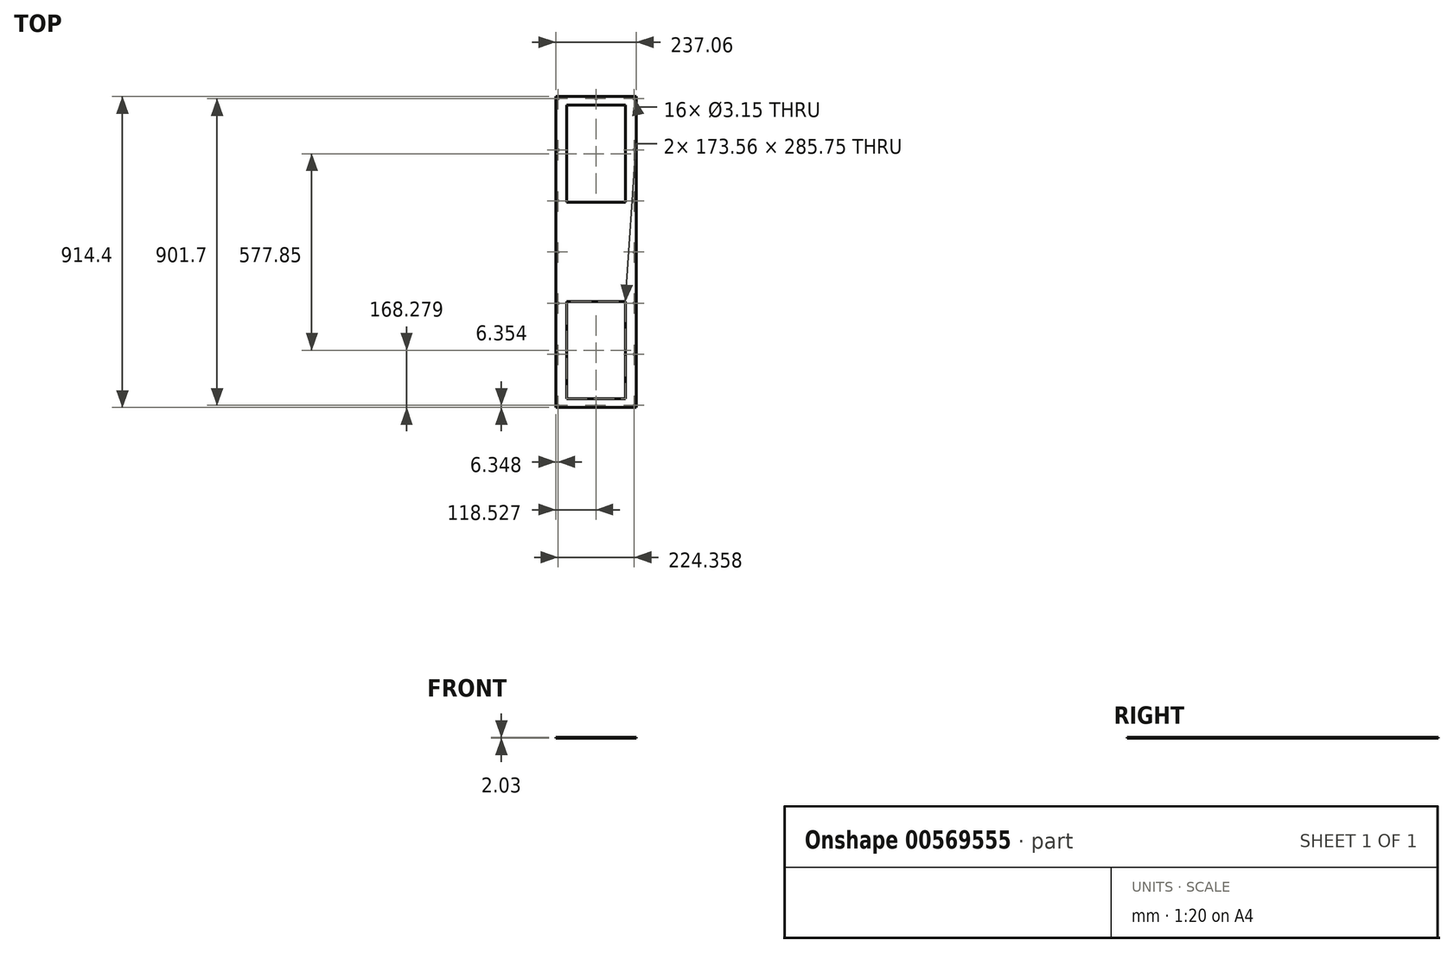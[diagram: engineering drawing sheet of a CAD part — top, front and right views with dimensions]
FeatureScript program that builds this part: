
annotation { "Feature Type Name" : "Feature", "Feature Type Description" : "" }
export const myFeature = defineFeature(function(context is Context, id is Id, definition is map)
    precondition{}
    {
        {
            var Q0;
            Q0=qCreatedBy(makeId("Top.planeOp"),FACE);
            var sketch = newSketch(context, id + "F0", { "sketchPlane" : qUnion([Q0])});
            skLineSegment(sketch, "E0.bottom", {"start": v(-468.83, 456.62) * mm, "end": v(-231.77, 456.62) * mm});
            skLineSegment(sketch, "E0.top", {"start": v(-468.83, -457.78) * mm, "end": v(-231.77, -457.78) * mm});
            skLineSegment(sketch, "E0.left", {"start": v(-468.83, 456.62) * mm, "end": v(-468.83, -457.78) * mm});
            skLineSegment(sketch, "E0.right", {"start": v(-231.77, 456.62) * mm, "end": v(-231.77, -457.78) * mm});
            skLineSegment(sketch, "E1.bottom", {"start": v(-437.08, 431.22) * mm, "end": v(-263.52, 431.22) * mm});
            skLineSegment(sketch, "E1.top", {"start": v(-437.08, 145.47) * mm, "end": v(-263.52, 145.47) * mm});
            skLineSegment(sketch, "E1.left", {"start": v(-437.08, 431.22) * mm, "end": v(-437.08, 145.47) * mm});
            skLineSegment(sketch, "E1.right", {"start": v(-263.52, 431.22) * mm, "end": v(-263.52, 145.47) * mm});
            skLineSegment(sketch, "E2.bottom", {"start": v(-437.08, -146.63) * mm, "end": v(-263.52, -146.63) * mm});
            skLineSegment(sketch, "E2.top", {"start": v(-437.08, -432.38) * mm, "end": v(-263.52, -432.38) * mm});
            skLineSegment(sketch, "E2.left", {"start": v(-437.08, -146.63) * mm, "end": v(-437.08, -432.38) * mm});
            skLineSegment(sketch, "E2.right", {"start": v(-263.52, -146.63) * mm, "end": v(-263.52, -432.38) * mm});
            skLineSegment(sketch, "E3", {"start": v(-468.83, -0.58) * mm, "end": v(-231.77, -0.58) * mm, "construction": true});
            skLineSegment(sketch, "E4", {"start": v(-350.3, 456.62) * mm, "end": v(-350.3, -457.78) * mm, "construction": true});
            skLineSegment(sketch, "E5.0", {"start": v(-462.48, 450.27) * mm, "end": v(-462.48, -451.43) * mm, "construction": true});
            skLineSegment(sketch, "E5.1", {"start": v(-462.48, 450.27) * mm, "end": v(-238.12, 450.27) * mm, "construction": true});
            skLineSegment(sketch, "E5.2", {"start": v(-238.12, 450.27) * mm, "end": v(-238.12, -451.43) * mm, "construction": true});
            skLineSegment(sketch, "E5.3", {"start": v(-462.48, -451.43) * mm, "end": v(-238.12, -451.43) * mm, "construction": true});
            skCircle(sketch, "E6", {"center": v(-462.48, 450.27) * mm, "radius": 1.57 * mm});
            skCircle(sketch, "E7", {"center": v(-462.48, -451.43) * mm, "radius": 1.57 * mm});
            skCircle(sketch, "E8", {"center": v(-238.12, -451.43) * mm, "radius": 1.57 * mm});
            skCircle(sketch, "E9", {"center": v(-238.12, 450.27) * mm, "radius": 1.57 * mm});
            skCircle(sketch, "E10", {"center": v(-350.3, 450.27) * mm, "radius": 1.57 * mm});
            skCircle(sketch, "E11", {"center": v(-350.3, -451.43) * mm, "radius": 1.57 * mm});
            skCircle(sketch, "E12", {"center": v(-462.48, -0.58) * mm, "radius": 1.57 * mm});
            skCircle(sketch, "E13", {"center": v(-238.12, -0.58) * mm, "radius": 1.57 * mm});
            skLineSegment(sketch, "E14.0", {"start": v(-468.83, 149.7) * mm, "end": v(-231.77, 149.7) * mm, "construction": true});
            skLineSegment(sketch, "E15.0", {"start": v(-468.83, 300) * mm, "end": v(-231.77, 300) * mm, "construction": true});
            skCircle(sketch, "E16", {"center": v(-462.48, 300) * mm, "radius": 1.57 * mm});
            skCircle(sketch, "E17", {"center": v(-462.48, 149.7) * mm, "radius": 1.57 * mm});
            skCircle(sketch, "E18", {"center": v(-238.12, 300) * mm, "radius": 1.57 * mm});
            skCircle(sketch, "E19", {"center": v(-238.12, 149.7) * mm, "radius": 1.57 * mm});
            skCircle(sketch, "E20.MirrorC", {"center": v(-462.48, -150.86) * mm, "radius": 1.57 * mm});
            skCircle(sketch, "E21.MirrorC", {"center": v(-238.12, -150.86) * mm, "radius": 1.57 * mm});
            skCircle(sketch, "E22.MirrorC", {"center": v(-238.12, -301.14) * mm, "radius": 1.57 * mm});
            skCircle(sketch, "E23.MirrorC", {"center": v(-462.48, -301.14) * mm, "radius": 1.57 * mm});
            skPoint(sketch, "E24.middle", {"position": v(-350.3, 300) * mm});
            skLineSegment(sketch, "E25.0", {"start": v(-437.08, 133.4) * mm, "end": v(-263.52, 133.4) * mm, "construction": true});
            skLineSegment(sketch, "E26.0", {"start": v(-437.08, -134.56) * mm, "end": v(-263.52, -134.56) * mm, "construction": true});
            skSolve(sketch);
        }
        {
            var Q0;
            Q0=makeQuery(id+"F0.imprint","IMPRINT",FACE,{"disambiguationData":[TD([[makeQuery(id+"F0.imprint","IMPRINT",EDGE,{"derivedFrom":sQuery(id+"F0.wireOp",EDGE,"E0.bottom")}),-1.0]])]});
            extrude(context, id + "F1", {"entities" : qUnion([Q0]), "depth" : 2.03 * mm, "offsetDistance" : 25.4 * mm});
        }
    });
